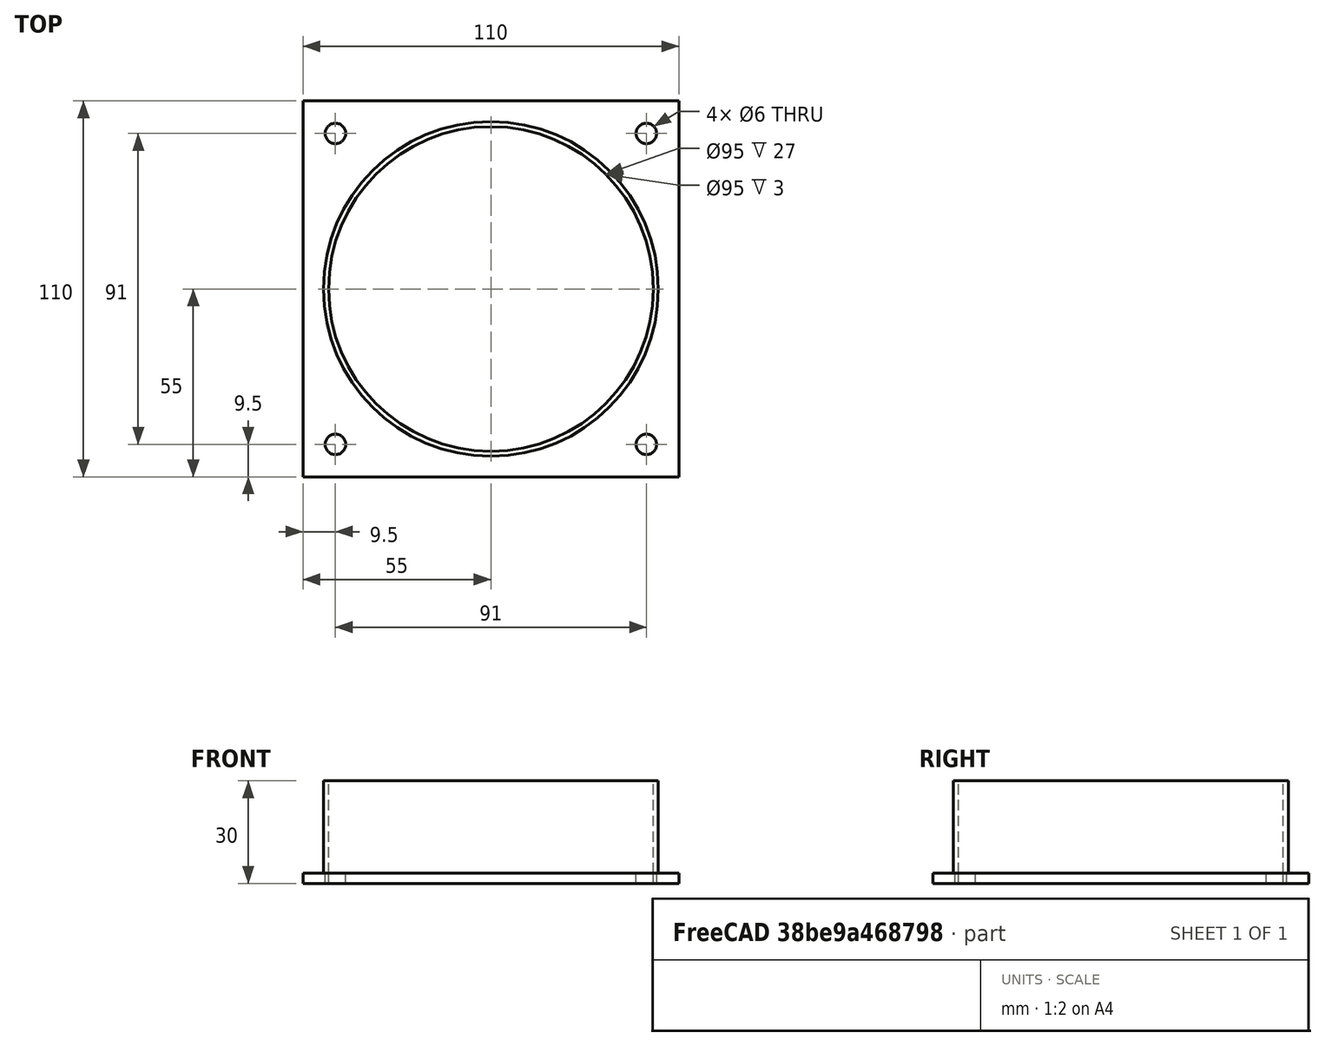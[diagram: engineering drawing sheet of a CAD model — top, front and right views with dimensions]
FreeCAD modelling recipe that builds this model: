
FCSTD DOCUMENT  (FreeCAD 0.18.4R)
Label: substrat_holder
License: All rights reserved
LicenseURL: http://en.wikipedia.org/wiki/All_rights_reserved
objects: Part::Cylinder×6, Part::Cut×6, Part::Box×1, Part::MultiFuse×1
note: 14 computed .brp shape members not serialized (recipe doc carries the construction recipe); baked Part::Feature solids carry a one-line shape summary decoded from their .brp

FEATURE [Part::Box] Box  label="Cube"
  AttacherType = Attacher::AttachEngine3D
  Height = 3
  Length = 110
  Width = 110
FEATURE [Part::Cylinder] Cylinder
  Angle = 360
  AttacherType = Attacher::AttachEngine3D
  Height = 30
  Placement = pos=(55,55,0) rot=(0,0,1;0rad)
  Radius = 49
FEATURE [Part::Cylinder] Cylinder001
  Angle = 360
  AttacherType = Attacher::AttachEngine3D
  Height = 30
  Placement = pos=(55,55,0) rot=(0,0,1;0rad)
  Radius = 47.5
FEATURE [Part::Cut] Cut
  Base = -> Box
  Tool = -> Cylinder001
FEATURE [Part::Cut] Cut001
  Base = -> Cylinder
  Tool = -> Cylinder001
FEATURE [Part::MultiFuse] Fusion
  Shapes = -> [Cut001,Cut]
FEATURE [Part::Cylinder] Cylinder002
  Angle = 360
  AttacherType = Attacher::AttachEngine3D
  Height = 10
  Placement = pos=(9.5,9.5,0) rot=(0,0,1;0rad)
  Radius = 3
FEATURE [Part::Cylinder] Cylinder003
  Angle = 360
  AttacherType = Attacher::AttachEngine3D
  Height = 10
  Placement = pos=(9.5,100.5,0) rot=(0,0,1;0rad)
  Radius = 3
FEATURE [Part::Cylinder] Cylinder004
  Angle = 360
  AttacherType = Attacher::AttachEngine3D
  Height = 10
  Placement = pos=(100.5,100.5,0) rot=(0,0,1;0rad)
  Radius = 3
FEATURE [Part::Cylinder] Cylinder005
  Angle = 360
  AttacherType = Attacher::AttachEngine3D
  Height = 10
  Placement = pos=(100.5,9.5,0) rot=(0,0,1;0rad)
  Radius = 3
FEATURE [Part::Cut] Cut002
  Base = -> Fusion
  Tool = -> Cylinder002
FEATURE [Part::Cut] Cut003
  Base = -> Cut002
  Tool = -> Cylinder003
FEATURE [Part::Cut] Cut004
  Base = -> Cut003
  Tool = -> Cylinder004
FEATURE [Part::Cut] Cut005
  Base = -> Cut004
  Tool = -> Cylinder005
